# Revit family: Roofing-Aquaknight-Butynol_Dropper
name_source: partatom
category: Pipe Accessories
revit_build: Autodesk Revit 2016 (Build: 20150714_1515(x64)
units: mm (PartAtom-declared; Revit-internal decimal feet)

## family parameters
Always vertical = Yes
Cut with Voids When Loaded = No
OmniClass Number = 23.60.30.11
OmniClass Title = Pipework Products for General Use
Part Type = Normal
Round Connector Dimension = Use Diameter
Shared = No
Work Plane-Based = No

## types (3) — shared parameters
250mm Head Flow = 0.0 L/s
400mm Head Flow = 0.0 L/s
Manufacturer = Aquaknight Industries Ltd
URL = www.aquaknight.co.nz

## per-type parameters (varying)
| type | Connector Diameter | DN | Depth | Description | Drain Diameter | Drain Interior Diameter | Drain Interior Radius | Drain Radius | Extrusion End | Length | Max Weir Flow | Model | Pipe Joint Location | Width |
| DN100 | 100 mm  [stored 0.328084 ft] | 100 | 204 mm | Butynol Dropper 300x100 | 100 mm  [stored 0.328084 ft] | 93 mm  [stored 0.305118 ft] | 46.5 mm  [stored 0.152559 ft] | 50 mm  [stored 0.164042 ft] | 3.5 mm  [stored 0.0114829 ft] | 299 mm  [stored 0.980971 ft] | 7.5 L/s | 2100.108 | 149.5 mm  [stored 0.490486 ft] | 204 mm |
| DN150 | 148 mm  [stored 0.485564 ft] | 150 | 277 mm  [stored 0.908793 ft] | Butynol Dropper 300x150 | 147.5 mm  [stored 0.483924 ft] | 140.5 mm  [stored 0.460958 ft] | 70.25 mm  [stored 0.230479 ft] | 73.75 mm  [stored 0.241962 ft] | 3.5 mm  [stored 0.0114829 ft] | 300 mm | 12.2 L/s | 2100.109 | 150 mm | 277 mm  [stored 0.908793 ft] |
| DN80 | 74 mm  [stored 0.242782 ft] | 80 | 204 mm | Butynol Dropper 300x80 | 73.5 mm  [stored 0.241142 ft] | 68.5 mm  [stored 0.224738 ft] | 34.25 mm  [stored 0.112369 ft] | 36.75 mm  [stored 0.120571 ft] | 2.5 mm  [stored 0.0082021 ft] | 298 mm  [stored 0.97769 ft] | 5.0 L/s | 2100.107 | 149 mm  [stored 0.488845 ft] | 204 mm |

note: [stored X ft] marks values corroborated as IEEE doubles in the binary element streams (Revit-internal decimal feet)

## geometry (parser evidence)
native form markers: Extrusion x1, Sweep x3
no freeform markers — native parametric forms only
